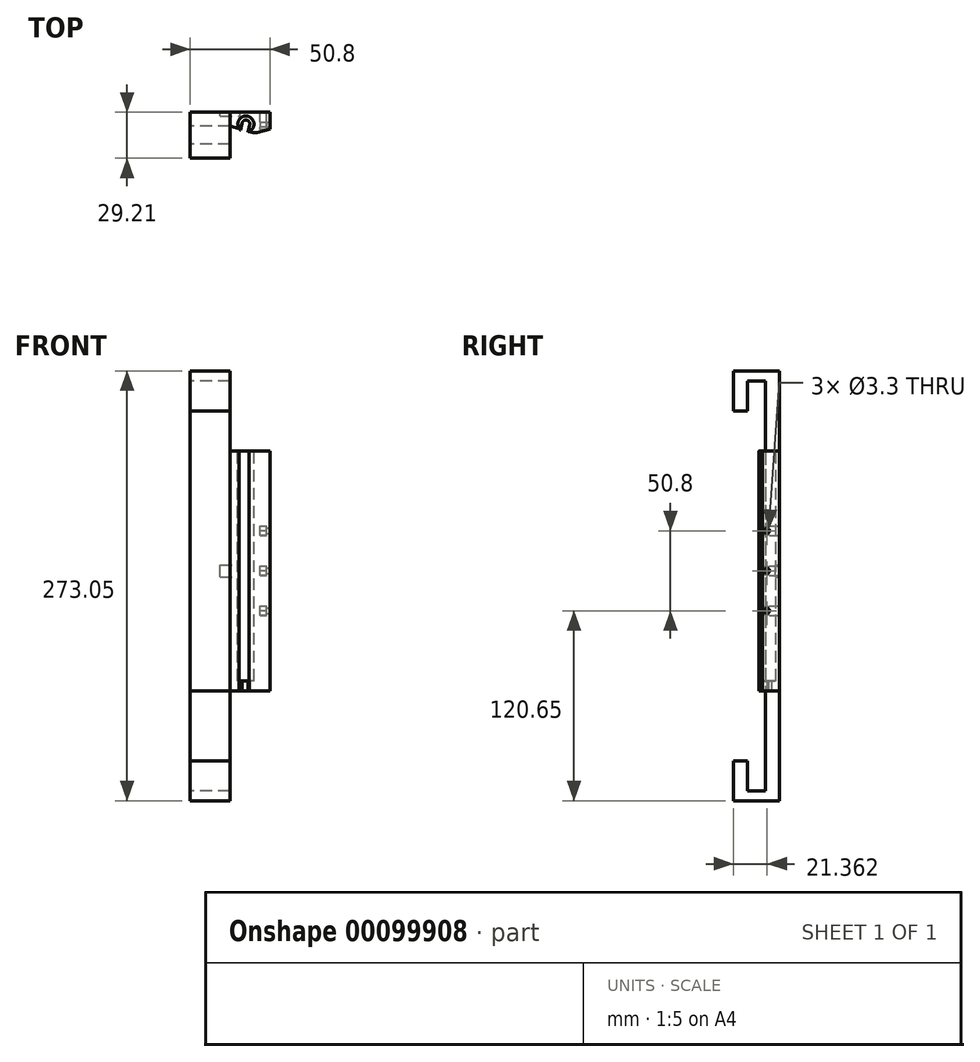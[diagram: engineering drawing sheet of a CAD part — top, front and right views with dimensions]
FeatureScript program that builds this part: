
annotation { "Feature Type Name" : "Feature", "Feature Type Description" : "" }
export const myFeature = defineFeature(function(context is Context, id is Id, definition is map)
    precondition{}
    {
        {
            var Q0;
            Q0=qCreatedBy(makeId("Right.planeOp"),FACE);
            var sketch = newSketch(context, id + "F0", { "sketchPlane" : qUnion([Q0])});
            skLineSegment(sketch, "E0", {"start": v(0, 0) * mm, "end": v(0, 203.2) * mm});
            skLineSegment(sketch, "E1", {"start": v(0, 203.2) * mm, "end": v(-29.21, 203.2) * mm});
            skLineSegment(sketch, "E2", {"start": v(-29.21, 203.2) * mm, "end": v(-29.21, 177.8) * mm});
            skLineSegment(sketch, "E3", {"start": v(-29.21, 177.8) * mm, "end": v(-20.32, 177.8) * mm});
            skLineSegment(sketch, "E4", {"start": v(-20.32, 177.8) * mm, "end": v(-20.32, 196.85) * mm});
            skLineSegment(sketch, "E5", {"start": v(-20.32, 196.85) * mm, "end": v(-8.9, 196.85) * mm});
            skLineSegment(sketch, "E6", {"start": v(-8.9, 196.85) * mm, "end": v(-8.89, 0) * mm});
            skLineSegment(sketch, "E7", {"start": v(-8.89, 0) * mm, "end": v(0, 0) * mm});
            skSolve(sketch);
        }
        {
            var Q0;
            Q0 = qSketchRegion(id + "F0", true);
            extrude(context, id + "F1", {"entities" : qUnion([Q0]), "depth" : 25.4 * mm});
        }
        {
            var Q0;
            Q0=qCreatedBy(makeId("Top.planeOp"),FACE);
            var sketch = newSketch(context, id + "F2", { "sketchPlane" : qUnion([Q0])});
            skLineSegment(sketch, "E8", {"start": v(25.4, 0) * mm, "end": v(50.8, 0) * mm});
            skLineSegment(sketch, "E9", {"start": v(50.8, 0) * mm, "end": v(50.8, -15.7) * mm});
            skLineSegment(sketch, "E10", {"start": v(50.8, -15.7) * mm, "end": v(25.4, -8.89) * mm});
            skLineSegment(sketch, "E11", {"start": v(25.4, -8.89) * mm, "end": v(25.4, 0) * mm});
            skSolve(sketch);
        }
        {
            var Q0;
            Q0 = qSketchRegion(id + "F2", true);
            extrude(context, id + "F3", {"entities" : qUnion([Q0]), "operationType" : NewBodyOperationType.ADD, "depth" : 152.4 * mm});
        }
        {
            var Q0;
            Q0=makeQuery(id+"F3.opExtrude","CAP_FACE",FACE,{"disambiguationData":[OSD([sQuery(id+"F2.wireOp",EDGE,"E8"),sQuery(id+"F2.wireOp",EDGE,"E9"),sQuery(id+"F2.wireOp",EDGE,"E10"),sQuery(id+"F2.wireOp",EDGE,"E11")])],"isStart":false});
            var sketch = newSketch(context, id + "F4", { "sketchPlane" : qUnion([Q0])});
            skCircle(sketch, "E12", {"center": v(35.46, -7.48) * mm, "radius": 5.14 * mm});
            skSolve(sketch);
        }
        {
            var Q0;
            Q0 = qSketchRegion(id + "F4", true);
            extrude(context, id + "F5", {"entities" : qUnion([Q0]), "operationType" : NewBodyOperationType.REMOVE, "endBound" : BoundingType.THROUGH_ALL, "oppositeDirection" : true, "depth" : 25.4 * mm});
        }
        {
            var Q0;
            Q0=makeQuery(id+"F3.boolean.opBoolean","MERGE",FACE,{"derivedFrom":[makeQuery(id+"F1.opExtrude","SWEPT_FACE",FACE,{"disambiguationData":[OSD([sQuery(id+"F0.wireOp",EDGE,"E7")])]}),makeQuery(id+"F3.opExtrude","CAP_FACE",FACE,{"disambiguationData":[OSD([sQuery(id+"F2.wireOp",EDGE,"E8"),sQuery(id+"F2.wireOp",EDGE,"E9"),sQuery(id+"F2.wireOp",EDGE,"E10"),sQuery(id+"F2.wireOp",EDGE,"E11")])],"isStart":true})]});
            var sketch = newSketch(context, id + "F6", { "sketchPlane" : qUnion([Q0])});
            skArc(sketch, "E13", {"start": v(31.94, 11.23) * mm, "mid": v(36.67, 2.49) * mm, "end": v(36.88, 12.42) * mm});
            skArc(sketch, "E14", {"start": v(32.98, 6.93) * mm, "mid": v(36.06, 5.02) * mm, "end": v(37.92, 8.12) * mm});
            skLineSegment(sketch, "E15", {"start": v(32.98, 6.93) * mm, "end": v(31.94, 11.23) * mm});
            skLineSegment(sketch, "E16", {"start": v(37.94, 8.04) * mm, "end": v(36.88, 12.42) * mm});
            skSolve(sketch);
        }
        {
            var Q0;
            Q0=makeQuery(id+"F3.opExtrude","SWEPT_FACE",FACE,{"disambiguationData":[OSD([sQuery(id+"F2.wireOp",EDGE,"E9")])]});
            cPlane(context, id + "F7", {"entities" : qUnion([Q0]), "cplaneType" : CPlaneType.OFFSET, "offset" : 6.35 * mm, "oppositeDirection" : true, "width" : 152.4 * mm, "height" : 152.4 * mm});
        }
        {
            var Q0;
            Q0=qCreatedBy(id+"F7.planeOp",FACE);
            var sketch = newSketch(context, id + "F8", { "sketchPlane" : qUnion([Q0])});
            skCircle(sketch, "E17.cCircle", {"center": v(-7.85, 101.6) * mm, "radius": 2.8 * mm, "construction": true});
            skLineSegment(sketch, "E17.0", {"start": v(-6.24, 104.4) * mm, "end": v(-4.62, 101.6) * mm});
            skLineSegment(sketch, "E17.1", {"start": v(-4.62, 101.6) * mm, "end": v(-6.24, 98.8) * mm});
            skLineSegment(sketch, "E17.2", {"start": v(-6.24, 98.8) * mm, "end": v(-9.46, 98.8) * mm});
            skLineSegment(sketch, "E17.3", {"start": v(-9.46, 98.8) * mm, "end": v(-11.07, 101.6) * mm});
            skLineSegment(sketch, "E17.4", {"start": v(-11.07, 101.6) * mm, "end": v(-9.46, 104.4) * mm});
            skLineSegment(sketch, "E17.5", {"start": v(-9.46, 104.4) * mm, "end": v(-6.24, 104.4) * mm});
            skPoint(sketch, "E17.0.midPoint", {"position": v(-5.43, 103) * mm});
            skPoint(sketch, "E18", {"position": v(-7.85, 152.4) * mm});
            skLineSegment(sketch, "E19.0.1.0", {"start": v(-9.46, 79) * mm, "end": v(-6.24, 79) * mm});
            skLineSegment(sketch, "E19.0.1.1", {"start": v(-4.62, 76.2) * mm, "end": v(-6.24, 73.4) * mm});
            skLineSegment(sketch, "E19.0.1.2", {"start": v(-6.24, 73.4) * mm, "end": v(-9.46, 73.4) * mm});
            skCircle(sketch, "E19.0.1.3", {"center": v(-7.85, 76.2) * mm, "radius": 2.8 * mm, "construction": true});
            skLineSegment(sketch, "E19.0.1.4", {"start": v(-9.46, 73.4) * mm, "end": v(-11.07, 76.2) * mm});
            skLineSegment(sketch, "E19.0.1.5", {"start": v(-11.07, 76.2) * mm, "end": v(-9.46, 79) * mm});
            skPoint(sketch, "E19.0.1.6", {"position": v(-5.43, 77.6) * mm});
            skLineSegment(sketch, "E19.0.1.7", {"start": v(-6.24, 79) * mm, "end": v(-4.62, 76.2) * mm});
            skLineSegment(sketch, "E19.0.2.0", {"start": v(-9.46, 53.6) * mm, "end": v(-6.24, 53.6) * mm});
            skLineSegment(sketch, "E19.0.2.1", {"start": v(-4.62, 50.8) * mm, "end": v(-6.24, 48) * mm});
            skLineSegment(sketch, "E19.0.2.2", {"start": v(-6.24, 48) * mm, "end": v(-9.46, 48) * mm});
            skCircle(sketch, "E19.0.2.3", {"center": v(-7.85, 50.8) * mm, "radius": 2.8 * mm, "construction": true});
            skLineSegment(sketch, "E19.0.2.4", {"start": v(-9.46, 48) * mm, "end": v(-11.07, 50.8) * mm});
            skLineSegment(sketch, "E19.0.2.5", {"start": v(-11.07, 50.8) * mm, "end": v(-9.46, 53.6) * mm});
            skPoint(sketch, "E19.0.2.6", {"position": v(-5.43, 52.2) * mm});
            skLineSegment(sketch, "E19.0.2.7", {"start": v(-6.24, 53.6) * mm, "end": v(-4.62, 50.8) * mm});
            skLineSegment(sketch, "E19.direction1", {"start": v(-9.46, 104.4) * mm, "end": v(15.94, 104.4) * mm, "construction": true});
            skLineSegment(sketch, "E19.direction2", {"start": v(-9.46, 104.4) * mm, "end": v(-9.46, 79) * mm, "construction": true});
            skSolve(sketch);
        }
        {
            var Q0;
            Q0 = qSketchRegion(id + "F8", true);
            extrude(context, id + "F9", {"entities" : qUnion([Q0]), "operationType" : NewBodyOperationType.REMOVE, "depth" : 4.06 * mm});
        }
        {
            var Q0;
            Q0=makeQuery(id+"F3.opExtrude","SWEPT_FACE",FACE,{"disambiguationData":[OSD([sQuery(id+"F2.wireOp",EDGE,"E9")])]});
            var sketch = newSketch(context, id + "F10", { "sketchPlane" : qUnion([Q0])});
            skCircle(sketch, "E20", {"center": v(-7.85, 101.6) * mm, "radius": 1.65 * mm});
            skPoint(sketch, "E20.centerSnap0", {"position": v(-7.85, 152.4) * mm});
            skCircle(sketch, "E21.0.1.0", {"center": v(-7.85, 76.2) * mm, "radius": 1.65 * mm});
            skCircle(sketch, "E21.0.2.0", {"center": v(-7.85, 50.8) * mm, "radius": 1.65 * mm});
            skLineSegment(sketch, "E21.direction1", {"start": v(-7.85, 101.6) * mm, "end": v(17.55, 101.6) * mm, "construction": true});
            skLineSegment(sketch, "E21.direction2", {"start": v(-7.85, 101.6) * mm, "end": v(-7.85, 76.2) * mm, "construction": true});
            skSolve(sketch);
        }
        {
            var Q0;
            Q0 = qSketchRegion(id + "F10", true);
            extrude(context, id + "F11", {"entities" : qUnion([Q0]), "operationType" : NewBodyOperationType.REMOVE, "endBound" : BoundingType.UP_TO_NEXT, "oppositeDirection" : true, "depth" : 25.4 * mm});
        }
        {
            var Q0;
            Q0=makeQuery(id+"F3.boolean.opBoolean","MERGE",FACE,{"derivedFrom":[makeQuery(id+"F1.opExtrude","SWEPT_FACE",FACE,{"disambiguationData":[OSD([sQuery(id+"F0.wireOp",EDGE,"E0")])]}),makeQuery(id+"F3.opExtrude","SWEPT_FACE",FACE,{"disambiguationData":[OSD([sQuery(id+"F2.wireOp",EDGE,"E8")])]})]});
            var sketch = newSketch(context, id + "F12", { "sketchPlane" : qUnion([Q0])});
            skLineSegment(sketch, "E22", {"start": v(-50.8, 152.4) * mm, "end": v(-44.45, 152.4) * mm, "construction": true});
            skLineSegment(sketch, "E23", {"start": v(-44.45, 152.4) * mm, "end": v(-44.45, 101.6) * mm, "construction": true});
            skLineSegment(sketch, "E24.bottom", {"start": v(-44.45, 98.62) * mm, "end": v(-48.51, 98.62) * mm});
            skLineSegment(sketch, "E24.top", {"start": v(-44.45, 104.58) * mm, "end": v(-48.51, 104.58) * mm});
            skLineSegment(sketch, "E24.left", {"start": v(-44.45, 98.62) * mm, "end": v(-44.45, 104.58) * mm});
            skLineSegment(sketch, "E24.right", {"start": v(-48.51, 98.62) * mm, "end": v(-48.51, 104.58) * mm});
            skLineSegment(sketch, "E25.0.1.0", {"start": v(-44.45, 73.22) * mm, "end": v(-48.51, 73.22) * mm});
            skLineSegment(sketch, "E25.0.1.1", {"start": v(-44.45, 79.18) * mm, "end": v(-48.51, 79.18) * mm});
            skLineSegment(sketch, "E25.0.1.2", {"start": v(-48.51, 73.22) * mm, "end": v(-48.51, 79.18) * mm});
            skLineSegment(sketch, "E25.0.1.3", {"start": v(-44.45, 73.22) * mm, "end": v(-44.45, 79.18) * mm});
            skLineSegment(sketch, "E25.0.2.0", {"start": v(-44.45, 47.82) * mm, "end": v(-48.51, 47.82) * mm});
            skLineSegment(sketch, "E25.0.2.1", {"start": v(-44.45, 53.78) * mm, "end": v(-48.51, 53.78) * mm});
            skLineSegment(sketch, "E25.0.2.2", {"start": v(-48.51, 47.82) * mm, "end": v(-48.51, 53.78) * mm});
            skLineSegment(sketch, "E25.0.2.3", {"start": v(-44.45, 47.82) * mm, "end": v(-44.45, 53.78) * mm});
            skLineSegment(sketch, "E25.direction1", {"start": v(-48.51, 98.62) * mm, "end": v(-23.11, 98.62) * mm, "construction": true});
            skLineSegment(sketch, "E25.direction2", {"start": v(-48.51, 98.62) * mm, "end": v(-48.51, 73.22) * mm, "construction": true});
            skSolve(sketch);
        }
        {
            var Q0;
            Q0 = qSketchRegion(id + "F12", true);
            var Q1;
            Q1=makeQuery(id+"F9.boolean.opBoolean","COPY",FACE,{"derivedFrom":makeQuery(id+"F9.opExtrude","SWEPT_FACE",FACE,{"disambiguationData":[OSD([sQuery(id+"F8.wireOp",EDGE,"E17.1")])]})});
            var Q2;
            Q2=makeQuery(id+"F1.opExtrude","SWEPT_BODY",BODY,{"disambiguationData":[OSD([sQuery(id+"F0.wireOp",EDGE,"E0"),sQuery(id+"F0.wireOp",EDGE,"E1"),sQuery(id+"F0.wireOp",EDGE,"E2"),sQuery(id+"F0.wireOp",EDGE,"E3"),sQuery(id+"F0.wireOp",EDGE,"E4"),sQuery(id+"F0.wireOp",EDGE,"E5"),sQuery(id+"F0.wireOp",EDGE,"E6"),sQuery(id+"F0.wireOp",EDGE,"E7")])]});
            var Q3;
            Q3=makeQuery(id+"F9.boolean.opBoolean","COPY",FACE,{"derivedFrom":makeQuery(id+"F9.opExtrude","SWEPT_FACE",FACE,{"disambiguationData":[OSD([sQuery(id+"F8.wireOp",EDGE,"E17.0")])]})});
            extrude(context, id + "F13", {"entities" : qUnion([Q0]), "operationType" : NewBodyOperationType.REMOVE, "oppositeDirection" : true, "endBoundEntityFace" : qUnion([Q1]), "endBoundEntityBody" : qUnion([Q2]), "depth" : 6.35 * mm});
        }
        {
            var Q0;
            Q0 = qSketchRegion(id + "F6", true);
            extrude(context, id + "F14", {"entities" : qUnion([Q0]), "operationType" : NewBodyOperationType.ADD, "oppositeDirection" : true, "depth" : 6.35 * mm});
        }
        {
            var Q0;
            Q0=makeQuery(id+"F1.opExtrude","CAP_FACE",FACE,{"disambiguationData":[OSD([sQuery(id+"F0.wireOp",EDGE,"E0"),sQuery(id+"F0.wireOp",EDGE,"E1"),sQuery(id+"F0.wireOp",EDGE,"E2"),sQuery(id+"F0.wireOp",EDGE,"E3"),sQuery(id+"F0.wireOp",EDGE,"E4"),sQuery(id+"F0.wireOp",EDGE,"E5"),sQuery(id+"F0.wireOp",EDGE,"E6"),sQuery(id+"F0.wireOp",EDGE,"E7")])],"isStart":true});
            var sketch = newSketch(context, id + "F15", { "sketchPlane" : qUnion([Q0])});
            skLineSegment(sketch, "E26", {"start": v(8.89, 0) * mm, "end": v(0, 0) * mm});
            skLineSegment(sketch, "E27", {"start": v(0, 0) * mm, "end": v(0, -69.85) * mm});
            skLineSegment(sketch, "E28", {"start": v(0, -69.85) * mm, "end": v(29.2, -69.85) * mm});
            skLineSegment(sketch, "E29", {"start": v(29.2, -69.85) * mm, "end": v(29.2, -44.45) * mm});
            skLineSegment(sketch, "E30", {"start": v(29.2, -44.45) * mm, "end": v(20.32, -44.45) * mm});
            skLineSegment(sketch, "E31", {"start": v(20.32, -44.45) * mm, "end": v(20.32, -63.5) * mm});
            skLineSegment(sketch, "E32", {"start": v(20.32, -63.5) * mm, "end": v(8.89, -63.5) * mm});
            skLineSegment(sketch, "E33", {"start": v(8.89, -63.5) * mm, "end": v(8.89, 0) * mm});
            skSolve(sketch);
        }
        {
            var Q0;
            Q0 = qSketchRegion(id + "F15", true);
            extrude(context, id + "F16", {"entities" : qUnion([Q0]), "oppositeDirection" : true, "depth" : 25.4 * mm});
        }
        {
            var Q0;
            Q0=makeQuery(id+"F3.opExtrude","SWEPT_EDGE",EDGE,{"disambiguationData":[OSD([sQuery(id+"F2.wireOp",EDGE,"E9"),sQuery(id+"F2.wireOp",EDGE,"E10")])]});
            chamfer(context, id + "F17", {"entities" : qUnion([Q0]), "chamferType" : ChamferType.OFFSET_ANGLE, "width" : 5.08 * mm, "oppositeDirection" : false, "angle" : 75 * degree, "tangentPropagation" : true});
        }
        {
            var Q0;
            {var subQ0=sQuery(id+"F2.wireOp",EDGE,"E9");var subQ2=sQuery(id+"F2.wireOp",EDGE,"E10");Q0=makeQuery(id+"F17.opChamfer","BLEND_EDGE",EDGE,{"blendedFrom":[makeQuery(id+"F3.opExtrude","SWEPT_EDGE",EDGE,{"disambiguationData":[OSD([subQ0,subQ2])]}),makeQuery(id+"F5.boolean.opBoolean","SPLIT",FACE,{"disambiguationData":[TD([makeQuery(id+"F3.opExtrude","SWEPT_FACE",FACE,{"disambiguationData":[OSD([subQ0])]})])],"derivedFrom":makeQuery(id+"F3.opExtrude","SWEPT_FACE",FACE,{"disambiguationData":[OSD([subQ2])]})})],"blendedInto":[makeQuery(id+"F5.boolean.opBoolean","SPLIT",FACE,{"disambiguationData":[TD([makeQuery(id+"F3.opExtrude","SWEPT_FACE",FACE,{"disambiguationData":[OSD([subQ0])]})])],"derivedFrom":makeQuery(id+"F3.opExtrude","SWEPT_FACE",FACE,{"disambiguationData":[OSD([subQ2])]})})]});}
            fillet(context, id + "F18", {"entities" : qUnion([Q0]), "radius" : 5.08 * mm, "tangentPropagation" : true, "allowEdgeOverflow" : false});
        }
        {
            var Q0;
            Q0=makeQuery(id+"F3.boolean.opBoolean","MERGE",FACE,{"derivedFrom":[makeQuery(id+"F1.opExtrude","SWEPT_FACE",FACE,{"disambiguationData":[OSD([sQuery(id+"F0.wireOp",EDGE,"E0")])]}),makeQuery(id+"F3.opExtrude","SWEPT_FACE",FACE,{"disambiguationData":[OSD([sQuery(id+"F2.wireOp",EDGE,"E8")])]})]});
            var sketch = newSketch(context, id + "F19", { "sketchPlane" : qUnion([Q0])});
            skLineSegment(sketch, "E34", {"start": v(-25.4, 152.4) * mm, "end": v(-25.4, 76.2) * mm, "construction": true});
            skLineSegment(sketch, "E35.bottom", {"start": v(-19.05, 72.4) * mm, "end": v(-31.75, 72.4) * mm});
            skLineSegment(sketch, "E35.top", {"start": v(-19.05, 80.01) * mm, "end": v(-31.75, 80.01) * mm});
            skLineSegment(sketch, "E35.left", {"start": v(-19.05, 72.4) * mm, "end": v(-19.05, 80.01) * mm});
            skLineSegment(sketch, "E35.right", {"start": v(-31.75, 72.4) * mm, "end": v(-31.75, 80.01) * mm});
            skPoint(sketch, "E35.middle", {"position": v(-25.4, 76.2) * mm});
            skSolve(sketch);
        }
        {
            var Q0;
            Q0 = qSketchRegion(id + "F19", true);
            extrude(context, id + "F20", {"entities" : qUnion([Q0]), "operationType" : NewBodyOperationType.REMOVE, "oppositeDirection" : true, "depth" : 2.54 * mm});
        }
    });
